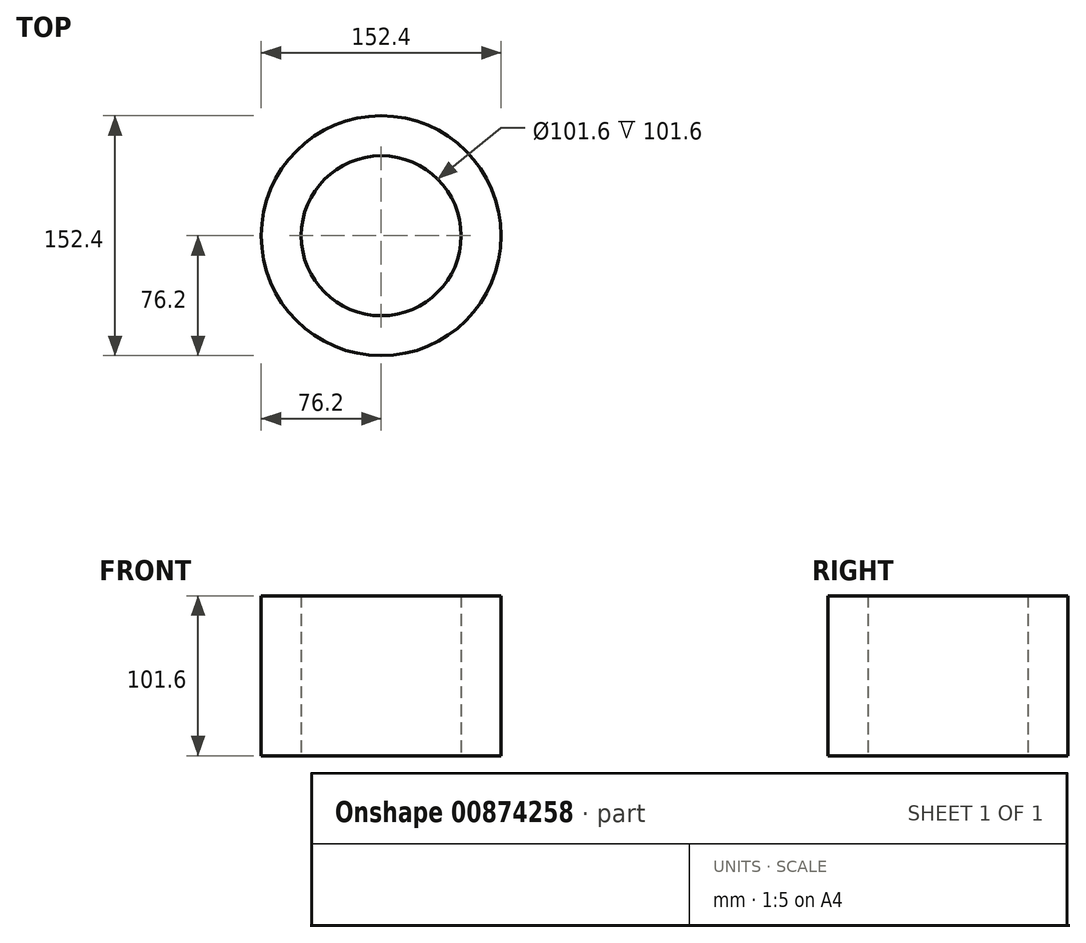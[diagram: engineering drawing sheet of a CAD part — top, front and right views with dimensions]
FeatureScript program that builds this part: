
annotation { "Feature Type Name" : "Feature", "Feature Type Description" : "" }
export const myFeature = defineFeature(function(context is Context, id is Id, definition is map)
    precondition{}
    {
        {
            var Q0;
            Q0=qCreatedBy(makeId("Top.planeOp"),FACE);
            var sketch = newSketch(context, id + "F0", { "sketchPlane" : qUnion([Q0])});
            skCircle(sketch, "E0", {"center": v(0, 0) * mm, "radius": 76.2 * mm});
            skCircle(sketch, "E1", {"center": v(0, 0) * mm, "radius": 50.8 * mm});
            skSolve(sketch);
        }
        {
            var Q0;
            Q0=makeQuery(id+"F0.imprint","IMPRINT",FACE,{"disambiguationData":[TD([[makeQuery(id+"F0.imprint","IMPRINT",EDGE,{"derivedFrom":sQuery(id+"F0.wireOp",EDGE,"E0")}),1.0]])]});
            extrude(context, id + "F1", {"entities" : qUnion([Q0]), "depth" : 101.6 * mm, "offsetDistance" : 25.4 * mm});
        }
    });
